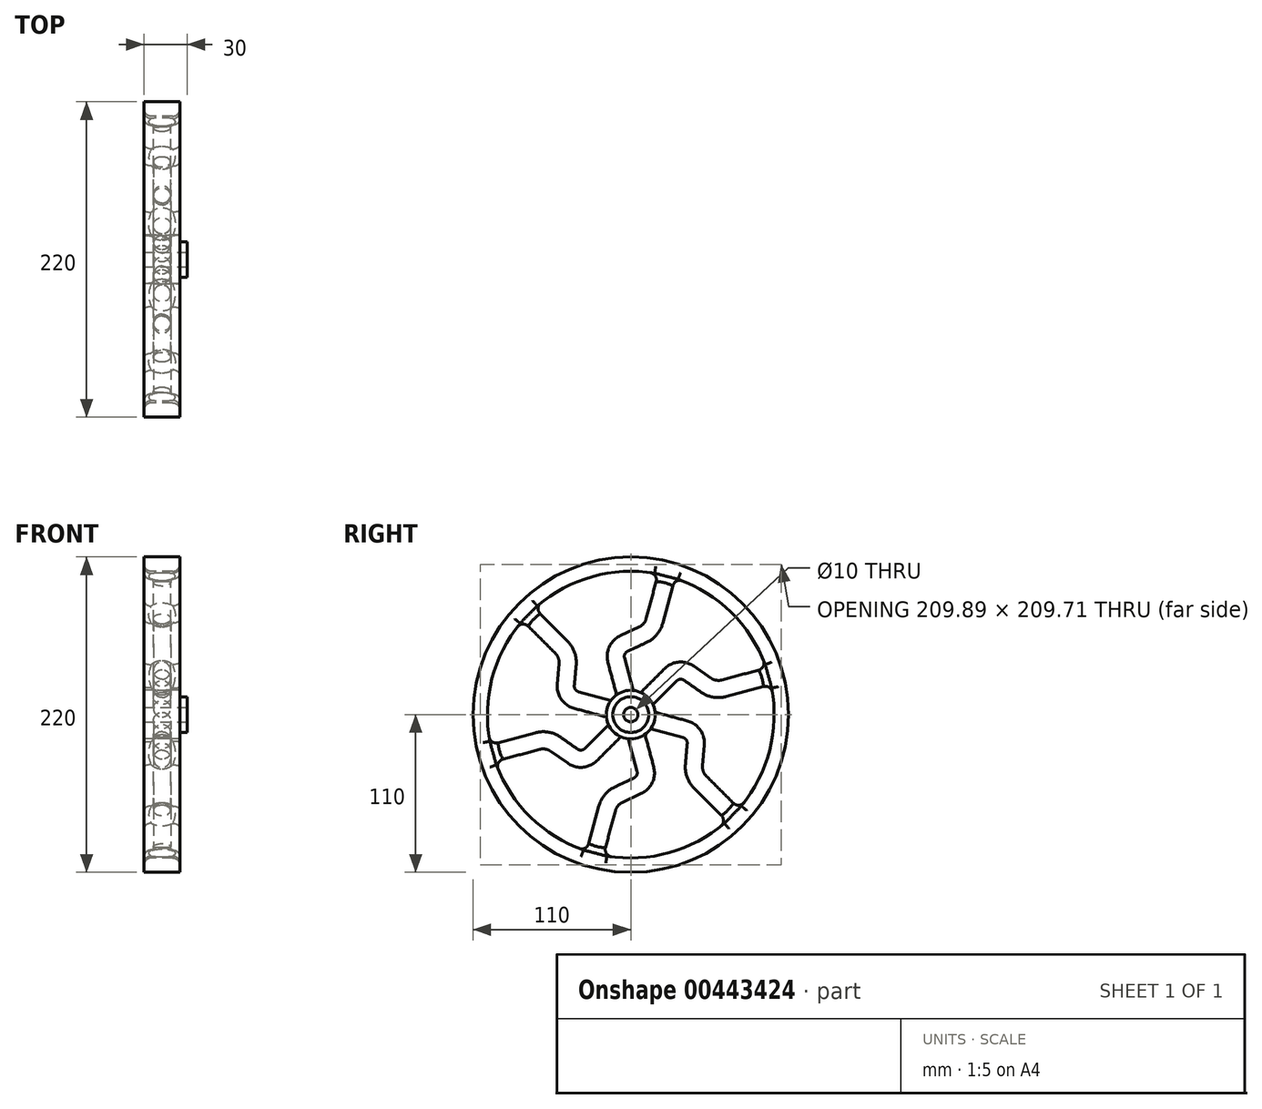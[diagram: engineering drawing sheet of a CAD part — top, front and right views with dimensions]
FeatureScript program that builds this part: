
annotation { "Feature Type Name" : "Feature", "Feature Type Description" : "" }
export const myFeature = defineFeature(function(context is Context, id is Id, definition is map)
    precondition{}
    {
        {
            var Q0;
            Q0=qCreatedBy(makeId("Right.planeOp"),FACE);
            var sketch = newSketch(context, id + "F0", { "sketchPlane" : qUnion([Q0])});
            skCircle(sketch, "E0", {"center": v(0, 0) * mm, "radius": 17 * mm});
            skSolve(sketch);
        }
        {
            var Q0;
            Q0 = qSketchRegion(id + "F0", true);
            extrude(context, id + "F1", {"entities" : qUnion([Q0]), "depth" : 25 * mm, "symmetric" : true});
        }
        {
            var Q0;
            Q0=makeQuery(id+"F1.opExtrude","CAP_FACE",FACE,{"disambiguationData":[OSD([sQuery(id+"F0.wireOp",EDGE,"E0")])],"isStart":false});
            var sketch = newSketch(context, id + "F2", { "sketchPlane" : qUnion([Q0])});
            skCircle(sketch, "E1", {"center": v(0, 0) * mm, "radius": 12.5 * mm});
            skSolve(sketch);
        }
        {
            var Q0;
            Q0=makeQuery(id+"F2.imprint","IMPRINT",FACE,{"disambiguationData":[TD([[makeQuery(id+"F2.imprint","IMPRINT",EDGE,{"derivedFrom":sQuery(id+"F2.wireOp",EDGE,"E1")}),1.0]])]});
            extrude(context, id + "F3", {"entities" : qUnion([Q0]), "operationType" : NewBodyOperationType.ADD, "depth" : 5 * mm});
        }
        {
            var Q0;
            Q0=makeQuery(id+"F3.opExtrude","CAP_FACE",FACE,{"disambiguationData":[OSD([sQuery(id+"F2.wireOp",EDGE,"E1")])],"isStart":false});
            var sketch = newSketch(context, id + "F4", { "sketchPlane" : qUnion([Q0])});
            skCircle(sketch, "E2", {"center": v(0, 0) * mm, "radius": 5 * mm});
            skSolve(sketch);
        }
        {
            var Q0;
            Q0=qCreatedBy(makeId("Right.planeOp"),FACE);
            var sketch = newSketch(context, id + "F5", { "sketchPlane" : qUnion([Q0])});
            skCircle(sketch, "E3", {"center": v(0, 0) * mm, "radius": 100 * mm});
            skCircle(sketch, "E4", {"center": v(0, 0) * mm, "radius": 110 * mm});
            skSolve(sketch);
        }
        {
            var Q0;
            Q0=makeQuery(id+"F5.imprint","IMPRINT",FACE,{"disambiguationData":[TD([[makeQuery(id+"F5.imprint","IMPRINT",EDGE,{"derivedFrom":sQuery(id+"F5.wireOp",EDGE,"E3")}),-1.0]])]});
            extrude(context, id + "F6", {"entities" : qUnion([Q0]), "depth" : 25 * mm, "symmetric" : true});
        }
        {
            var Q0;
            Q0=qCreatedBy(makeId("Right.planeOp"),FACE);
            var sketch = newSketch(context, id + "F7", { "sketchPlane" : qUnion([Q0])});
            skLineSegment(sketch, "E5", {"start": v(0, 0) * mm, "end": v(-10.18, 37.98) * mm});
            skLineSegment(sketch, "E6", {"start": v(-4.74, 49.63) * mm, "end": v(8.4, 55.75) * mm});
            skLineSegment(sketch, "E7", {"start": v(16.55, 65.47) * mm, "end": v(25.63, 99.36) * mm});
            skCircle(sketch, "E8.0", {"center": v(0, 0) * mm, "radius": 100 * mm});
            skPoint(sketch, "E9.visualSharp", {"position": v(-12.35, 46.08) * mm});
            skArc(sketch, "E9.filletArc", {"start": v(-4.74, 49.63) * mm, "mid": v(-9.58, 44.79) * mm, "end": v(-10.18, 37.98) * mm});
            skPoint(sketch, "E10.visualSharp", {"position": v(14.74, 58.71) * mm});
            skArc(sketch, "E10.filletArc", {"start": v(8.4, 55.75) * mm, "mid": v(13.55, 59.7) * mm, "end": v(16.55, 65.47) * mm});
            skLineSegment(sketch, "E11", {"start": v(0, 0) * mm, "end": v(0, 119.77) * mm, "construction": true});
            skSolve(sketch);
        }
        {
            var Q0;
            Q0=qCreatedBy(makeId("Top.planeOp"),FACE);
            var Q1;
            Q1=makeQuery(id+"F1.opExtrude","CAP_EDGE",EDGE,{"disambiguationData":[OSD([sQuery(id+"F0.wireOp",EDGE,"E0")])],"isStart":false});
            cPlane(context, id + "F8", {"entities" : qUnion([Q0, Q1]), "cplaneType" : CPlaneType.LINE_ANGLE, "offset" : 25 * mm, "angle" : 15 * degree, "width" : 150 * mm, "height" : 150 * mm});
        }
        {
            var Q0;
            Q0=qCreatedBy(id+"F8.planeOp",FACE);
            var sketch = newSketch(context, id + "F9", { "sketchPlane" : qUnion([Q0])});
            skCircle(sketch, "E12", {"center": v(0, 0) * mm, "radius": 6 * mm});
            skSolve(sketch);
        }
        {
            var Q0;
            Q0 = qSketchRegion(id + "F9", true);
            var Q1;
            Q1=sQuery(id+"F7.wireOp",EDGE,"E5");
            var Q2;
            Q2=sQuery(id+"F7.wireOp",EDGE,"E9.filletArc");
            var Q3;
            Q3=sQuery(id+"F7.wireOp",EDGE,"E6");
            var Q4;
            Q4=sQuery(id+"F7.wireOp",EDGE,"E10.filletArc");
            var Q5;
            Q5=sQuery(id+"F7.wireOp",EDGE,"E7");
            sweep(context, id + "F10", {"profiles" : qUnion([Q0]), "path" : qUnion([Q1, Q2, Q3, Q4, Q5])});
        }
        {
            var Q0;
            Q0=makeQuery(id+"F10.opSweep","SWEPT_BODY",BODY,{"disambiguationData":[OSD([sQuery(id+"F7.wireOp",EDGE,"E7"),sQuery(id+"F9.wireOp",EDGE,"E12")])]});
            var Q1;
            Q1=makeQuery(id+"F6.opExtrude","CAP_EDGE",EDGE,{"disambiguationData":[OSD([sQuery(id+"F5.wireOp",EDGE,"E4")])],"isStart":false});
            circularPattern(context, id + "F11", {"entities" : qUnion([Q0]), "axis" : qUnion([Q1]), "angle" : 360 * degree, "instanceCount" : 6, "equalSpace" : true});
        }
        {
            var Q0;
            Q0=makeQuery(id+"F6.opExtrude","SWEPT_BODY",BODY,{"disambiguationData":[OSD([sQuery(id+"F5.wireOp",EDGE,"E3"),sQuery(id+"F5.wireOp",EDGE,"E4")])]});
            var Q1;
            Q1=makeQuery(id+"F11.opPattern","COPY",BODY,{"derivedFrom":makeQuery(id+"F10.opSweep","SWEPT_BODY",BODY,{"disambiguationData":[OSD([sQuery(id+"F7.wireOp",EDGE,"E7"),sQuery(id+"F9.wireOp",EDGE,"E12")])]}),"instanceName":"4"});
            var Q2;
            Q2=makeQuery(id+"F11.opPattern","COPY",BODY,{"derivedFrom":makeQuery(id+"F10.opSweep","SWEPT_BODY",BODY,{"disambiguationData":[OSD([sQuery(id+"F7.wireOp",EDGE,"E7"),sQuery(id+"F9.wireOp",EDGE,"E12")])]}),"instanceName":"3"});
            var Q3;
            Q3=makeQuery(id+"F10.opSweep","SWEPT_BODY",BODY,{"disambiguationData":[OSD([sQuery(id+"F7.wireOp",EDGE,"E7"),sQuery(id+"F9.wireOp",EDGE,"E12")])]});
            var Q4;
            Q4=makeQuery(id+"F11.opPattern","COPY",BODY,{"derivedFrom":makeQuery(id+"F10.opSweep","SWEPT_BODY",BODY,{"disambiguationData":[OSD([sQuery(id+"F7.wireOp",EDGE,"E7"),sQuery(id+"F9.wireOp",EDGE,"E12")])]}),"instanceName":"1"});
            var Q5;
            Q5=makeQuery(id+"F11.opPattern","COPY",BODY,{"derivedFrom":makeQuery(id+"F10.opSweep","SWEPT_BODY",BODY,{"disambiguationData":[OSD([sQuery(id+"F7.wireOp",EDGE,"E7"),sQuery(id+"F9.wireOp",EDGE,"E12")])]}),"instanceName":"2"});
            var Q6;
            Q6=makeQuery(id+"F11.opPattern","COPY",BODY,{"derivedFrom":makeQuery(id+"F10.opSweep","SWEPT_BODY",BODY,{"disambiguationData":[OSD([sQuery(id+"F7.wireOp",EDGE,"E7"),sQuery(id+"F9.wireOp",EDGE,"E12")])]}),"instanceName":"5"});
            var Q7;
            Q7=makeQuery(id+"F1.opExtrude","SWEPT_BODY",BODY,{"disambiguationData":[OSD([sQuery(id+"F0.wireOp",EDGE,"E0")])]});
            booleanBodies(context, id + "F12", {"operationType" : BooleanOperationType.UNION, "tools" : qUnion([Q0, Q1, Q2, Q3, Q4, Q5, Q6, Q7])});
        }
        {
            var Q0;
            Q0=makeQuery(id+"F12.opBoolean","INTERSECT",EDGE,{"derivedFrom":[makeQuery(id+"F6.opExtrude","SWEPT_FACE",FACE,{"disambiguationData":[OSD([sQuery(id+"F5.wireOp",EDGE,"E3")])]}),makeQuery(id+"F10.opSweep","SWEPT_FACE",FACE,{"disambiguationData":[OSD([sQuery(id+"F7.wireOp",EDGE,"E7"),sQuery(id+"F9.wireOp",EDGE,"E12")])]})]});
            var Q1;
            Q1=makeQuery(id+"F12.opBoolean","INTERSECT",EDGE,{"derivedFrom":[makeQuery(id+"F6.opExtrude","SWEPT_FACE",FACE,{"disambiguationData":[OSD([sQuery(id+"F5.wireOp",EDGE,"E3")])]}),makeQuery(id+"F11.opPattern","COPY",FACE,{"derivedFrom":makeQuery(id+"F10.opSweep","SWEPT_FACE",FACE,{"disambiguationData":[OSD([sQuery(id+"F7.wireOp",EDGE,"E7"),sQuery(id+"F9.wireOp",EDGE,"E12")])]}),"instanceName":"1"})]});
            var Q2;
            Q2=makeQuery(id+"F12.opBoolean","INTERSECT",EDGE,{"derivedFrom":[makeQuery(id+"F6.opExtrude","SWEPT_FACE",FACE,{"disambiguationData":[OSD([sQuery(id+"F5.wireOp",EDGE,"E3")])]}),makeQuery(id+"F11.opPattern","COPY",FACE,{"derivedFrom":makeQuery(id+"F10.opSweep","SWEPT_FACE",FACE,{"disambiguationData":[OSD([sQuery(id+"F7.wireOp",EDGE,"E7"),sQuery(id+"F9.wireOp",EDGE,"E12")])]}),"instanceName":"5"})]});
            var Q3;
            Q3=makeQuery(id+"F12.opBoolean","INTERSECT",EDGE,{"derivedFrom":[makeQuery(id+"F6.opExtrude","SWEPT_FACE",FACE,{"disambiguationData":[OSD([sQuery(id+"F5.wireOp",EDGE,"E3")])]}),makeQuery(id+"F11.opPattern","COPY",FACE,{"derivedFrom":makeQuery(id+"F10.opSweep","SWEPT_FACE",FACE,{"disambiguationData":[OSD([sQuery(id+"F7.wireOp",EDGE,"E7"),sQuery(id+"F9.wireOp",EDGE,"E12")])]}),"instanceName":"2"})]});
            var Q4;
            Q4=makeQuery(id+"F12.opBoolean","INTERSECT",EDGE,{"derivedFrom":[makeQuery(id+"F6.opExtrude","SWEPT_FACE",FACE,{"disambiguationData":[OSD([sQuery(id+"F5.wireOp",EDGE,"E3")])]}),makeQuery(id+"F11.opPattern","COPY",FACE,{"derivedFrom":makeQuery(id+"F10.opSweep","SWEPT_FACE",FACE,{"disambiguationData":[OSD([sQuery(id+"F7.wireOp",EDGE,"E7"),sQuery(id+"F9.wireOp",EDGE,"E12")])]}),"instanceName":"3"})]});
            var Q5;
            Q5=makeQuery(id+"F12.opBoolean","INTERSECT",EDGE,{"derivedFrom":[makeQuery(id+"F6.opExtrude","SWEPT_FACE",FACE,{"disambiguationData":[OSD([sQuery(id+"F5.wireOp",EDGE,"E3")])]}),makeQuery(id+"F11.opPattern","COPY",FACE,{"derivedFrom":makeQuery(id+"F10.opSweep","SWEPT_FACE",FACE,{"disambiguationData":[OSD([sQuery(id+"F7.wireOp",EDGE,"E7"),sQuery(id+"F9.wireOp",EDGE,"E12")])]}),"instanceName":"4"})]});
            fillet(context, id + "F13", {"entities" : qUnion([Q0, Q1, Q2, Q3, Q4, Q5]), "radius" : 5 * mm, "tangentPropagation" : true, "allowEdgeOverflow" : false});
        }
        {
            var Q0;
            Q0=makeQuery(id+"F6.opExtrude","CAP_EDGE",EDGE,{"disambiguationData":[OSD([sQuery(id+"F5.wireOp",EDGE,"E3")])],"isStart":true});
            var Q1;
            Q1=makeQuery(id+"F6.opExtrude","CAP_EDGE",EDGE,{"disambiguationData":[OSD([sQuery(id+"F5.wireOp",EDGE,"E3")])],"isStart":false});
            fillet(context, id + "F14", {"entities" : qUnion([Q0, Q1]), "radius" : 5 * mm, "tangentPropagation" : true, "allowEdgeOverflow" : false});
        }
        {
            var Q0;
            Q0=makeQuery(id+"F4.imprint","IMPRINT",FACE,{"disambiguationData":[TD([[makeQuery(id+"F4.imprint","IMPRINT",EDGE,{"derivedFrom":sQuery(id+"F4.wireOp",EDGE,"E2")}),1.0]])]});
            extrude(context, id + "F15", {"entities" : qUnion([Q0]), "operationType" : NewBodyOperationType.REMOVE, "endBound" : BoundingType.THROUGH_ALL, "oppositeDirection" : true, "depth" : 25 * mm});
        }
    });
